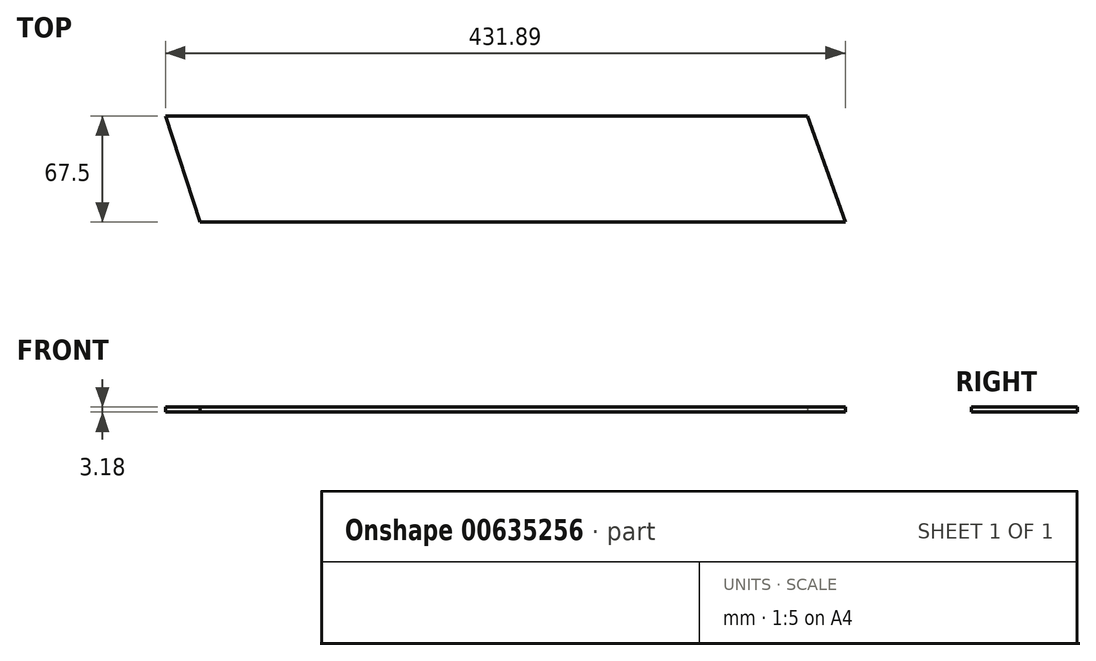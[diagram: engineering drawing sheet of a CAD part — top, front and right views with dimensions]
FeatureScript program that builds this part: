
annotation { "Feature Type Name" : "Feature", "Feature Type Description" : "" }
export const myFeature = defineFeature(function(context is Context, id is Id, definition is map)
    precondition{}
    {
        {
            var Q0;
            Q0=qCreatedBy(makeId("Top.planeOp"),FACE);
            var sketch = newSketch(context, id + "F0", { "sketchPlane" : qUnion([Q0])});
            skLineSegment(sketch, "E0.bottom", {"start": v(0, 0) * mm, "end": v(-431.9, 0) * mm});
            skLineSegment(sketch, "E0.top", {"start": v(-23.97, 67.5) * mm, "end": v(-431.9, 67.5) * mm});
            skLineSegment(sketch, "E0.left", {"start": v(0, 0) * mm, "end": v(0, 67.5) * mm});
            skLineSegment(sketch, "E0.right", {"start": v(-431.9, 0) * mm, "end": v(-431.9, 67.5) * mm});
            skLineSegment(sketch, "E1", {"start": v(-23.97, 67.5) * mm, "end": v(0, 0) * mm});
            skSolve(sketch);
        }
        {
            var Q0;
            Q0 = qSketchRegion(id + "F0", true);
            extrude(context, id + "F1", {"entities" : qUnion([Q0]), "depth" : 3.17 * mm, "offsetDistance" : 25.4 * mm});
        }
        {
            var Q0;
            Q0=makeQuery(id+"F1.opExtrude","CAP_FACE",FACE,{"disambiguationData":[OSD([sQuery(id+"F0.wireOp",EDGE,"E0.bottom"),sQuery(id+"F0.wireOp",EDGE,"E0.top"),sQuery(id+"F0.wireOp",EDGE,"E0.right"),sQuery(id+"F0.wireOp",EDGE,"E1")])],"isStart":false});
            var sketch = newSketch(context, id + "F2", { "sketchPlane" : qUnion([Q0])});
            skLineSegment(sketch, "E2", {"start": v(-431.9, 67.5) * mm, "end": v(-409.78, 0) * mm});
            skLineSegment(sketch, "E3", {"start": v(-409.78, 0) * mm, "end": v(-431.9, 0) * mm});
            skLineSegment(sketch, "E4", {"start": v(-431.9, 0) * mm, "end": v(-431.9, 67.5) * mm});
            skSolve(sketch);
        }
        {
            var Q0;
            Q0 = qSketchRegion(id + "F2", true);
            extrude(context, id + "F3", {"entities" : qUnion([Q0]), "operationType" : NewBodyOperationType.REMOVE, "oppositeDirection" : true, "depth" : 25.4 * mm, "offsetDistance" : 25.4 * mm});
        }
    });
